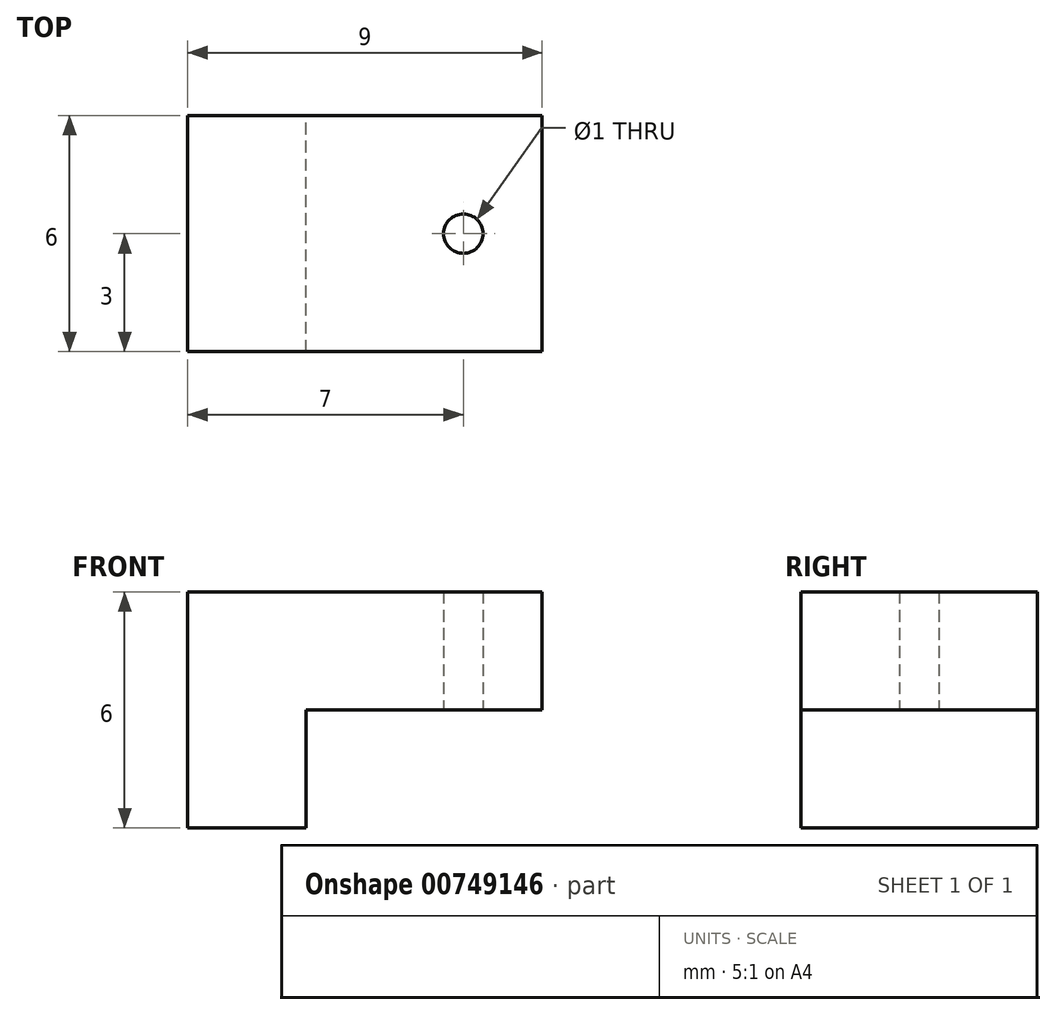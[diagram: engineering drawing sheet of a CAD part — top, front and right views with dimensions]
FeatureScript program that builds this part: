
annotation { "Feature Type Name" : "Feature", "Feature Type Description" : "" }
export const myFeature = defineFeature(function(context is Context, id is Id, definition is map)
    precondition{}
    {
        {
            var Q0;
            Q0=qCreatedBy(makeId("Top.planeOp"),FACE);
            var sketch = newSketch(context, id + "F0", { "sketchPlane" : qUnion([Q0])});
            skLineSegment(sketch, "E0", {"start": v(0, 0) * mm, "end": v(0, 6) * mm});
            skLineSegment(sketch, "E1", {"start": v(0, 6) * mm, "end": v(9, 6) * mm});
            skLineSegment(sketch, "E2", {"start": v(9, 6) * mm, "end": v(9, 0) * mm});
            skLineSegment(sketch, "E3", {"start": v(9, 0) * mm, "end": v(0, 0) * mm});
            skCircle(sketch, "E4", {"center": v(7, 3) * mm, "radius": 0.5 * mm});
            skPoint(sketch, "E4.centerSnap0", {"position": v(4.5, 0) * mm});
            skPoint(sketch, "E5", {"position": v(7, 0) * mm});
            skPoint(sketch, "E6", {"position": v(7, 6) * mm});
            skLineSegment(sketch, "E7", {"start": v(7, 6) * mm, "end": v(7, 0) * mm, "construction": true});
            skPoint(sketch, "E8", {"position": v(9, 3) * mm});
            skPoint(sketch, "E9", {"position": v(0, 3) * mm});
            skLineSegment(sketch, "E10", {"start": v(0, 3) * mm, "end": v(9, 3) * mm});
            skSolve(sketch);
        }
        {
            var Q0;
            {var subQ4=sQuery(id+"F0.wireOp",EDGE,"E3");Q0=makeQuery(id+"F0.imprint","IMPRINT",FACE,{"disambiguationData":[TD([[makeQuery(id+"F0.imprint","IMPRINT",EDGE,{"derivedFrom":subQ4}),-1.0]])]});}
            var Q1;
            {var subQ1=sQuery(id+"F0.wireOp",EDGE,"E1");Q1=makeQuery(id+"F0.imprint","IMPRINT",FACE,{"disambiguationData":[TD([[makeQuery(id+"F0.imprint","IMPRINT",EDGE,{"derivedFrom":subQ1}),-1.0]])]});}
            extrude(context, id + "F1", {"entities" : qUnion([Q0, Q1]), "depth" : 3 * mm, "offsetDistance" : 25 * mm});
        }
        {
            var Q0;
            Q0=qCreatedBy(makeId("Top.planeOp"),FACE);
            var sketch = newSketch(context, id + "F2", { "sketchPlane" : qUnion([Q0])});
            skLineSegment(sketch, "E11", {"start": v(3, 0) * mm, "end": v(3, 6) * mm});
            skLineSegment(sketch, "E12", {"start": v(3, 6) * mm, "end": v(0, 6) * mm});
            skLineSegment(sketch, "E13", {"start": v(0, 6) * mm, "end": v(0, 0) * mm});
            skLineSegment(sketch, "E14", {"start": v(0, 0) * mm, "end": v(3, 0) * mm});
            skSolve(sketch);
        }
        {
            var Q0;
            Q0 = qSketchRegion(id + "F2", true);
            extrude(context, id + "F3", {"entities" : qUnion([Q0]), "operationType" : NewBodyOperationType.ADD, "oppositeDirection" : true, "depth" : 3 * mm, "offsetDistance" : 25 * mm});
        }
    });
